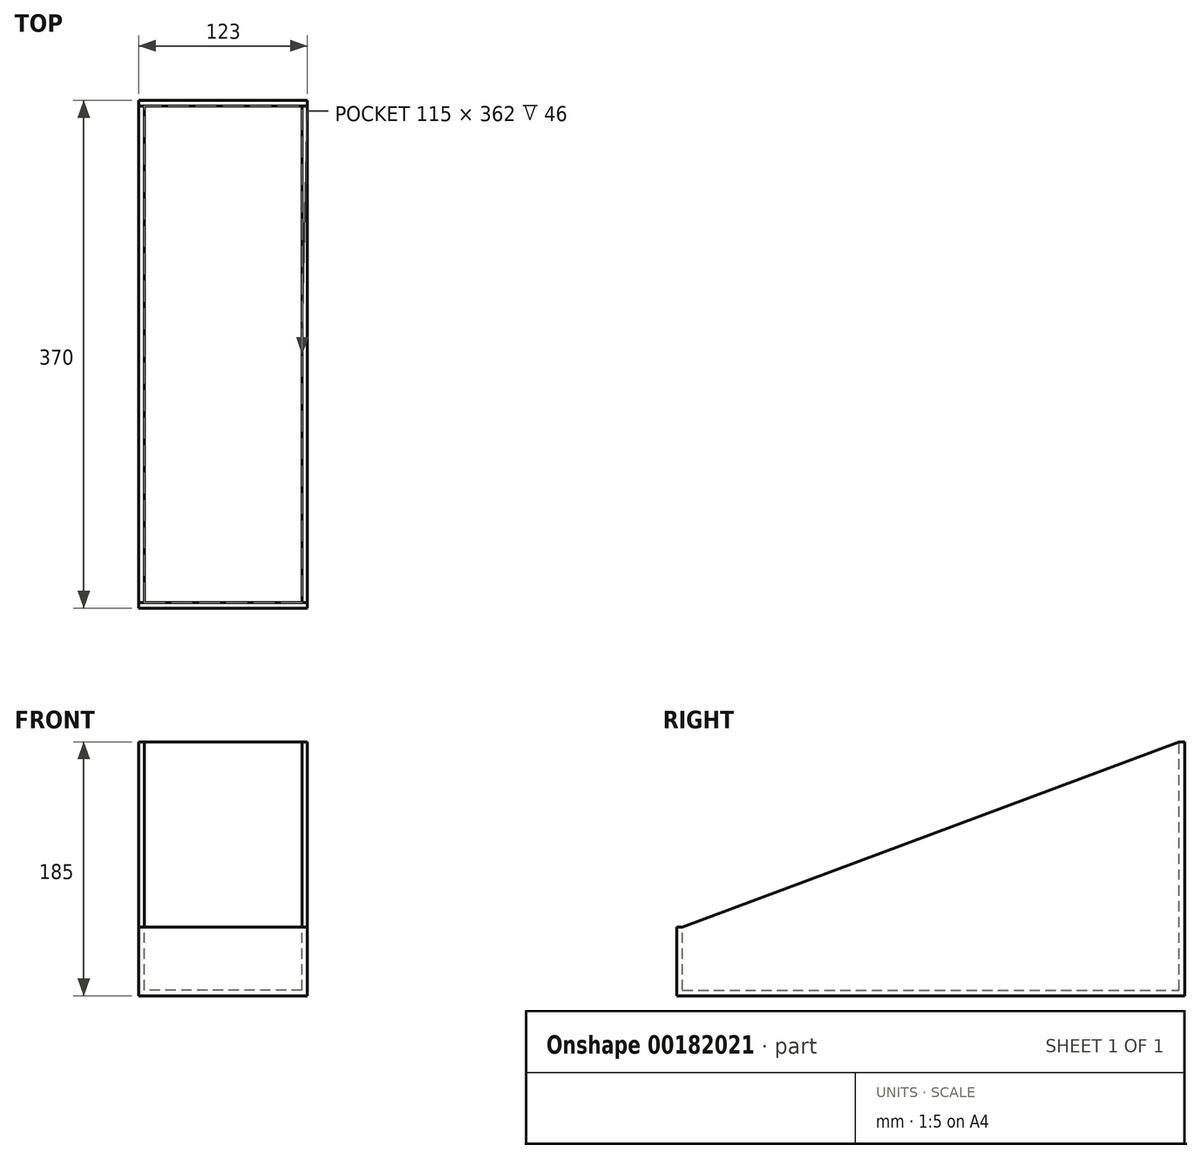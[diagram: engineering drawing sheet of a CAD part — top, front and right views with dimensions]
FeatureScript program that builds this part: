
annotation { "Feature Type Name" : "Feature", "Feature Type Description" : "" }
export const myFeature = defineFeature(function(context is Context, id is Id, definition is map)
    precondition{}
    {
        {
            var Q0;
            Q0=qCreatedBy(makeId("Front.planeOp"),FACE);
            var sketch = newSketch(context, id + "F0", { "sketchPlane" : qUnion([Q0])});
            skLineSegment(sketch, "E0.bottom", {"start": v(0, 0) * mm, "end": v(-123, 0) * mm});
            skLineSegment(sketch, "E0.top", {"start": v(0, 185) * mm, "end": v(-123, 185) * mm});
            skLineSegment(sketch, "E0.left", {"start": v(0, 0) * mm, "end": v(0, 185) * mm});
            skLineSegment(sketch, "E0.right", {"start": v(-123, 0) * mm, "end": v(-123, 185) * mm});
            skSolve(sketch);
        }
        {
            var Q0;
            Q0 = qSketchRegion(id + "F0", true);
            extrude(context, id + "F1", {"entities" : qUnion([Q0]), "oppositeDirection" : true, "depth" : 370 * mm});
        }
        {
            var Q0;
            Q0=qCreatedBy(makeId("Right.planeOp"),FACE);
            var sketch = newSketch(context, id + "F2", { "sketchPlane" : qUnion([Q0])});
            skLineSegment(sketch, "E1.0", {"start": v(370, 185) * mm, "end": v(0, 185) * mm, "construction": true});
            skLineSegment(sketch, "E2", {"start": v(0, 185) * mm, "end": v(0, 50) * mm});
            skLineSegment(sketch, "E3", {"start": v(0, 50) * mm, "end": v(4, 50) * mm});
            skLineSegment(sketch, "E4", {"start": v(4, 50) * mm, "end": v(366, 185) * mm});
            skLineSegment(sketch, "E5", {"start": v(366, 185) * mm, "end": v(0, 185) * mm});
            skSolve(sketch);
        }
        {
            var Q0;
            Q0=makeQuery(id+"F2.imprint","IMPRINT",FACE,{"disambiguationData":[TD([[makeQuery(id+"F2.imprint","IMPRINT",EDGE,{"derivedFrom":sQuery(id+"F2.wireOp",EDGE,"E2")}),1.0]])]});
            extrude(context, id + "F3", {"entities" : qUnion([Q0]), "operationType" : NewBodyOperationType.REMOVE, "endBound" : BoundingType.UP_TO_NEXT, "oppositeDirection" : true, "depth" : 25 * mm});
        }
        {
            var Q0;
            Q0=qCreatedBy(makeId("Top.planeOp"),FACE);
            cPlane(context, id + "F4", {"entities" : qUnion([Q0]), "cplaneType" : CPlaneType.OFFSET, "offset" : 200 * mm, "width" : 150 * mm, "height" : 150 * mm});
        }
        {
            var Q0;
            Q0=qCreatedBy(id+"F4.planeOp",FACE);
            var sketch = newSketch(context, id + "F5", { "sketchPlane" : qUnion([Q0])});
            skLineSegment(sketch, "E6.0.0", {"start": v(-123, 366) * mm, "end": v(-123, 4) * mm, "construction": true});
            skLineSegment(sketch, "E6.0.1", {"start": v(-123, 4) * mm, "end": v(0, 4) * mm, "construction": true});
            skLineSegment(sketch, "E6.0.2", {"start": v(0, 4) * mm, "end": v(0, 366) * mm, "construction": true});
            skLineSegment(sketch, "E6.0.3", {"start": v(0, 366) * mm, "end": v(-123, 366) * mm, "construction": true});
            skLineSegment(sketch, "E7.0", {"start": v(-4, 4) * mm, "end": v(-4, 366) * mm, "construction": true});
            skLineSegment(sketch, "E8.0", {"start": v(-119, 366) * mm, "end": v(-119, 4) * mm, "construction": true});
            skLineSegment(sketch, "E9.bottom", {"start": v(-4, 4) * mm, "end": v(-119, 4) * mm});
            skLineSegment(sketch, "E9.top", {"start": v(-4, 366) * mm, "end": v(-119, 366) * mm});
            skLineSegment(sketch, "E9.left", {"start": v(-4, 4) * mm, "end": v(-4, 366) * mm});
            skLineSegment(sketch, "E9.right", {"start": v(-119, 4) * mm, "end": v(-119, 366) * mm});
            skSolve(sketch);
        }
        {
            var Q0;
            Q0 = qSketchRegion(id + "F5", true);
            extrude(context, id + "F6", {"entities" : qUnion([Q0]), "operationType" : NewBodyOperationType.REMOVE, "oppositeDirection" : true, "depth" : 196 * mm});
        }
    });
